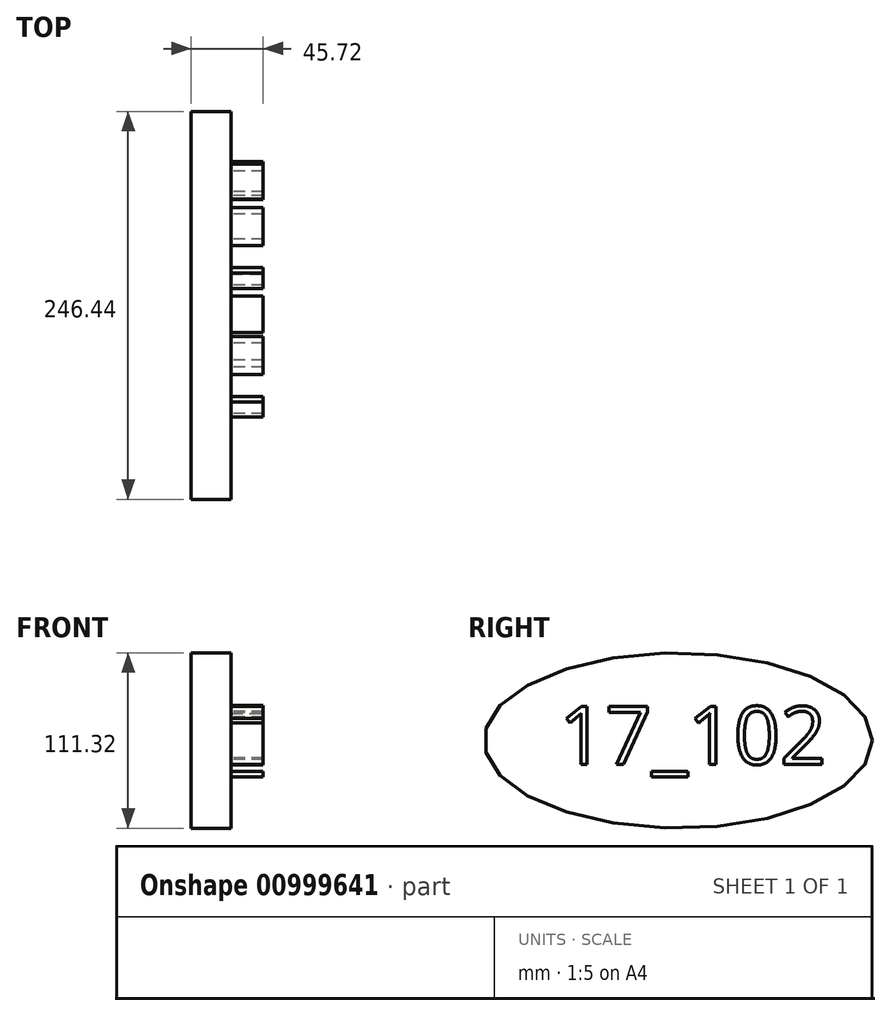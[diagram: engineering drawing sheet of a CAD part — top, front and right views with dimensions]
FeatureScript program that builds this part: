
annotation { "Feature Type Name" : "Feature", "Feature Type Description" : "" }
export const myFeature = defineFeature(function(context is Context, id is Id, definition is map)
    precondition{}
    {
        {
            var Q0;
            Q0=qCreatedBy(makeId("Right.planeOp"),FACE);
            var sketch = newSketch(context, id + "F0", { "sketchPlane" : qUnion([Q0])});
            skEllipse(sketch, "E0", {"center": v(0, 0) * mm, "majorRadius": 123.22 * mm, "minorRadius": 55.66 * mm, "majorAxis": v(1, 0)});
            skSolve(sketch);
        }
        {
            var Q0;
            Q0=makeQuery(id+"F0.imprint","IMPRINT",FACE,{"disambiguationData":[TD([[makeQuery(id+"F0.imprint","IMPRINT",EDGE,{"derivedFrom":sQuery(id+"F0.wireOp",EDGE,"E0")}),1.0]])]});
            extrude(context, id + "F1", {"entities" : qUnion([Q0]), "depth" : 25.4 * mm, "offsetDistance" : 25.4 * mm});
        }
        {
            var Q0;
            Q0=makeQuery(id+"F1.opExtrude","CAP_FACE",FACE,{"disambiguationData":[OSD([sQuery(id+"F0.wireOp",EDGE,"E0")])],"isStart":false});
            var sketch = newSketch(context, id + "F2", { "sketchPlane" : qUnion([Q0])});
            skText(sketch, "E1", { "text": "17_102", "fontName": "OpenSans-Regular.ttf"});
            const initialGuessF2  = {"E1": [-0.07571, -0.01506, 1, 0, 0.03696]};
            skSetInitialGuess(sketch, initialGuessF2);
            skSolve(sketch);
        }
        {
            var Q0;
            Q0 = qSketchRegion(id + "F2", true);
            extrude(context, id + "F3", {"entities" : qUnion([Q0]), "operationType" : NewBodyOperationType.ADD, "depth" : 20.32 * mm, "offsetDistance" : 25.4 * mm});
        }
    });
